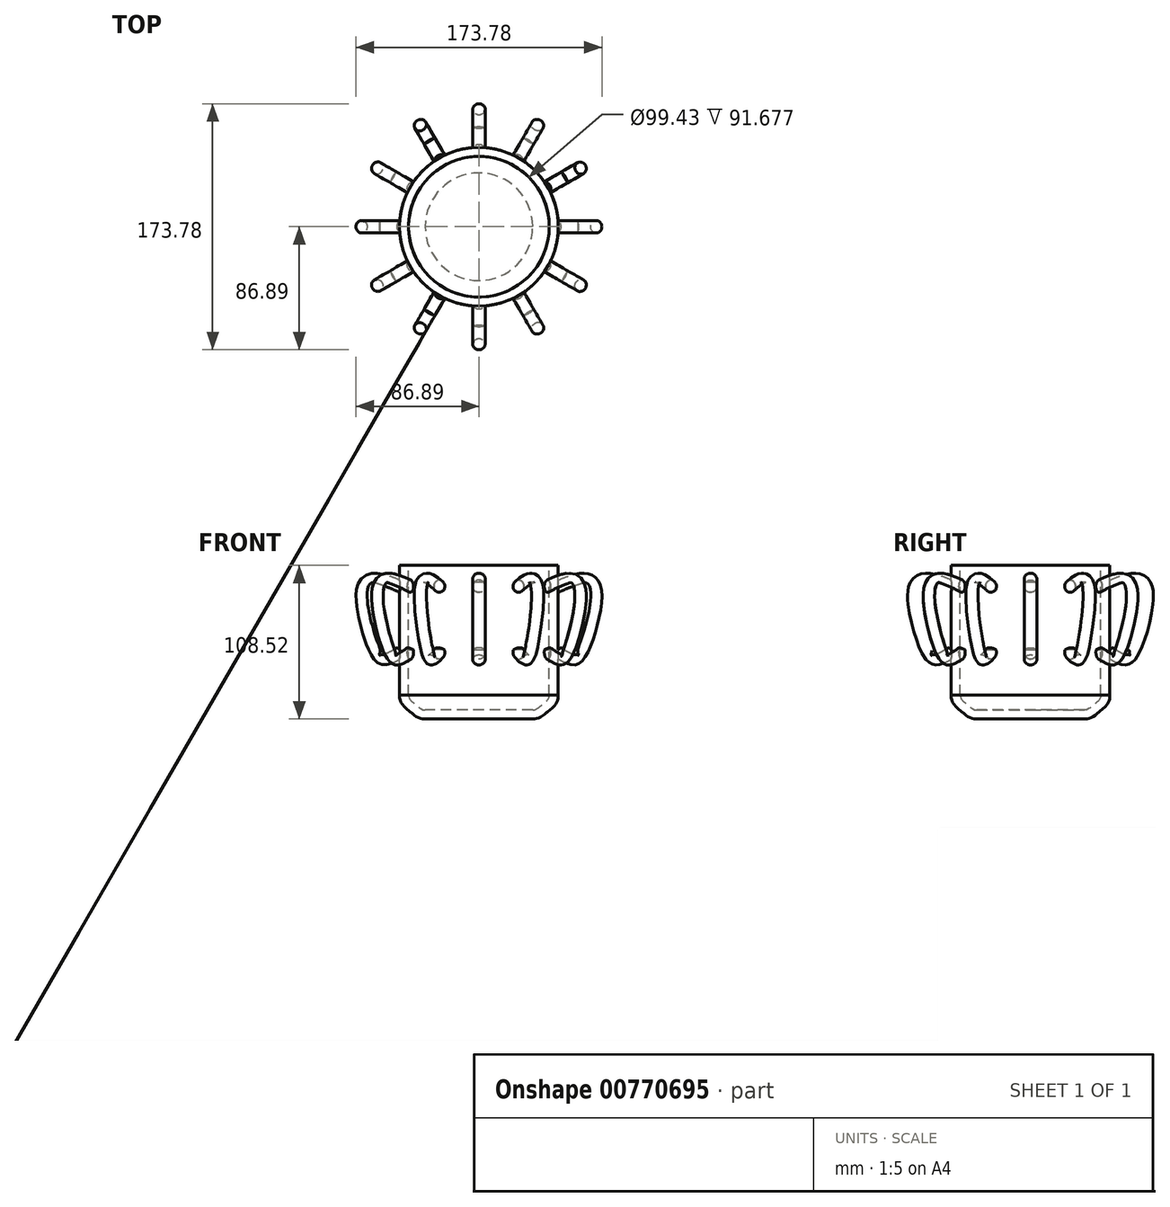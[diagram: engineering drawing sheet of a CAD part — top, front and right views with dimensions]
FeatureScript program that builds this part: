
annotation { "Feature Type Name" : "Feature", "Feature Type Description" : "" }
export const myFeature = defineFeature(function(context is Context, id is Id, definition is map)
    precondition{}
    {
        {
            var Q0;
            Q0=qCreatedBy(makeId("Front.planeOp"),FACE);
            var sketch = newSketch(context, id + "F0", { "sketchPlane" : qUnion([Q0])});
            skLineSegment(sketch, "E0", {"start": v(0, -23.02) * mm, "end": v(38.02, -23.02) * mm});
            skFitSpline(sketch, "E1", {"points": [v(38.02, -23.02) * mm, v(44.34, -19.54) * mm, v(49.72, -12.52) * mm], "startDerivative": vector(16.83, 0) * mm, "endDerivative": vector(0, 19.24) * mm});
            skLineSegment(sketch, "E2", {"start": v(49.72, -12.52) * mm, "end": v(49.72, 79.15) * mm});
            skLineSegment(sketch, "E3.0", {"start": v(56.07, -12.52) * mm, "end": v(56.07, 79.15) * mm});
            skFitSpline(sketch, "E3.1", {"points": [v(38.02, -29.37) * mm, v(38.75, -29.37) * mm, v(40.19, -29.24) * mm, v(42.17, -28.68) * mm, v(43.85, -27.89) * mm, v(45.21, -27.02) * mm, v(46.3, -26.18) * mm, v(47.05, -25.56) * mm, v(47.57, -25.12) * mm, v(47.87, -24.86) * mm, v(48.1, -24.68) * mm, v(48.26, -24.54) * mm, v(48.42, -24.42) * mm, v(48.65, -24.23) * mm, v(48.97, -23.98) * mm, v(49.56, -23.54) * mm, v(50.4, -22.9) * mm, v(51.53, -21.95) * mm, v(52.74, -20.77) * mm, v(53.97, -19.27) * mm, v(55.08, -17.38) * mm, v(55.88, -15.08) * mm, v(56.07, -13.38) * mm, v(56.07, -12.52) * mm]});
            skLineSegment(sketch, "E3.2", {"start": v(0, -29.37) * mm, "end": v(38.02, -29.37) * mm});
            skLineSegment(sketch, "E4", {"start": v(0, -23.02) * mm, "end": v(0, -29.37) * mm});
            skLineSegment(sketch, "E5", {"start": v(56.07, 79.15) * mm, "end": v(49.72, 79.15) * mm});
            skSolve(sketch);
        }
        {
            var Q0;
            Q0=qCreatedBy(makeId("Right.planeOp"),FACE);
            cPlane(context, id + "F1", {"entities" : qUnion([Q0]), "cplaneType" : CPlaneType.OFFSET, "offset" : 52.32 * mm, "width" : 152.4 * mm, "height" : 152.4 * mm});
        }
        {
            var Q0;
            Q0=qCreatedBy(id+"F1.planeOp",FACE);
            var sketch = newSketch(context, id + "F2", { "sketchPlane" : qUnion([Q0])});
            skCircle(sketch, "E6", {"center": v(0, 62.74) * mm, "radius": 4.42 * mm});
            skSolve(sketch);
        }
        {
            var Q0;
            Q0=qCreatedBy(makeId("Front.planeOp"),FACE);
            var sketch = newSketch(context, id + "F3", { "sketchPlane" : qUnion([Q0])});
            skFitSpline(sketch, "E7", {"points": [v(51.1, 66.6) * mm, v(60.32, 70.58) * mm, v(75.26, 73.57) * mm, v(85.72, 65.6) * mm, v(81.24, 28.5) * mm, v(68.79, 9.07) * mm, v(50.6, 16.3) * mm], "startDerivative": vector(69.43, 32.18) * mm, "endDerivative": vector(-115.9, 75.4) * mm});
            skLineSegment(sketch, "E8", {"start": v(0, 79.43) * mm, "end": v(0, -50.32) * mm});
            skLineSegment(sketch, "E9", {"start": v(50.6, 16.3) * mm, "end": v(48.57, 17.4) * mm});
            skSolve(sketch);
        }
        {
            var Q0;
            Q0=makeQuery(id+"F0.imprint","IMPRINT",FACE,{"disambiguationData":[TD([[makeQuery(id+"F0.imprint","IMPRINT",EDGE,{"derivedFrom":sQuery(id+"F0.wireOp",EDGE,"E0")}),-1.0]])]});
            var Q1;
            Q1=sQuery(id+"F3.wireOp",EDGE,"E8");
            revolve(context, id + "F4", {"surfaceOperationType" : NewSurfaceOperationType.NEW, "entities" : qUnion([Q0]), "axis" : qUnion([Q1]), "revolveType" : RevolveType.FULL});
        }
        {
            var Q0;
            Q0 = qSketchRegion(id + "F2", true);
            var Q1;
            Q1=sQuery(id+"F3.wireOp",EDGE,"E7");
            sweep(context, id + "F5", {"operationType" : NewBodyOperationType.ADD, "profiles" : qUnion([Q0]), "path" : qUnion([Q1])});
        }
        {
            var Q0;
            Q0=makeQuery(id+"F4.opRevolve","SWEPT_BODY",BODY,{"disambiguationData":[OSD([sQuery(id+"F0.wireOp",EDGE,"E0"),sQuery(id+"F0.wireOp",EDGE,"E1"),sQuery(id+"F0.wireOp",EDGE,"E2"),sQuery(id+"F0.wireOp",EDGE,"E3.0"),sQuery(id+"F0.wireOp",EDGE,"E3.1"),sQuery(id+"F0.wireOp",EDGE,"E3.2"),sQuery(id+"F0.wireOp",EDGE,"E4"),sQuery(id+"F0.wireOp",EDGE,"E5")])]});
            var Q1;
            Q1=sQuery(id+"F3.wireOp",EDGE,"E8");
            circularPattern(context, id + "F6", {"operationType" : NewBodyOperationType.ADD, "entities" : qUnion([Q0]), "axis" : qUnion([Q1]), "angle" : 360 * degree, "instanceCount" : 12, "equalSpace" : true});
        }
    });
